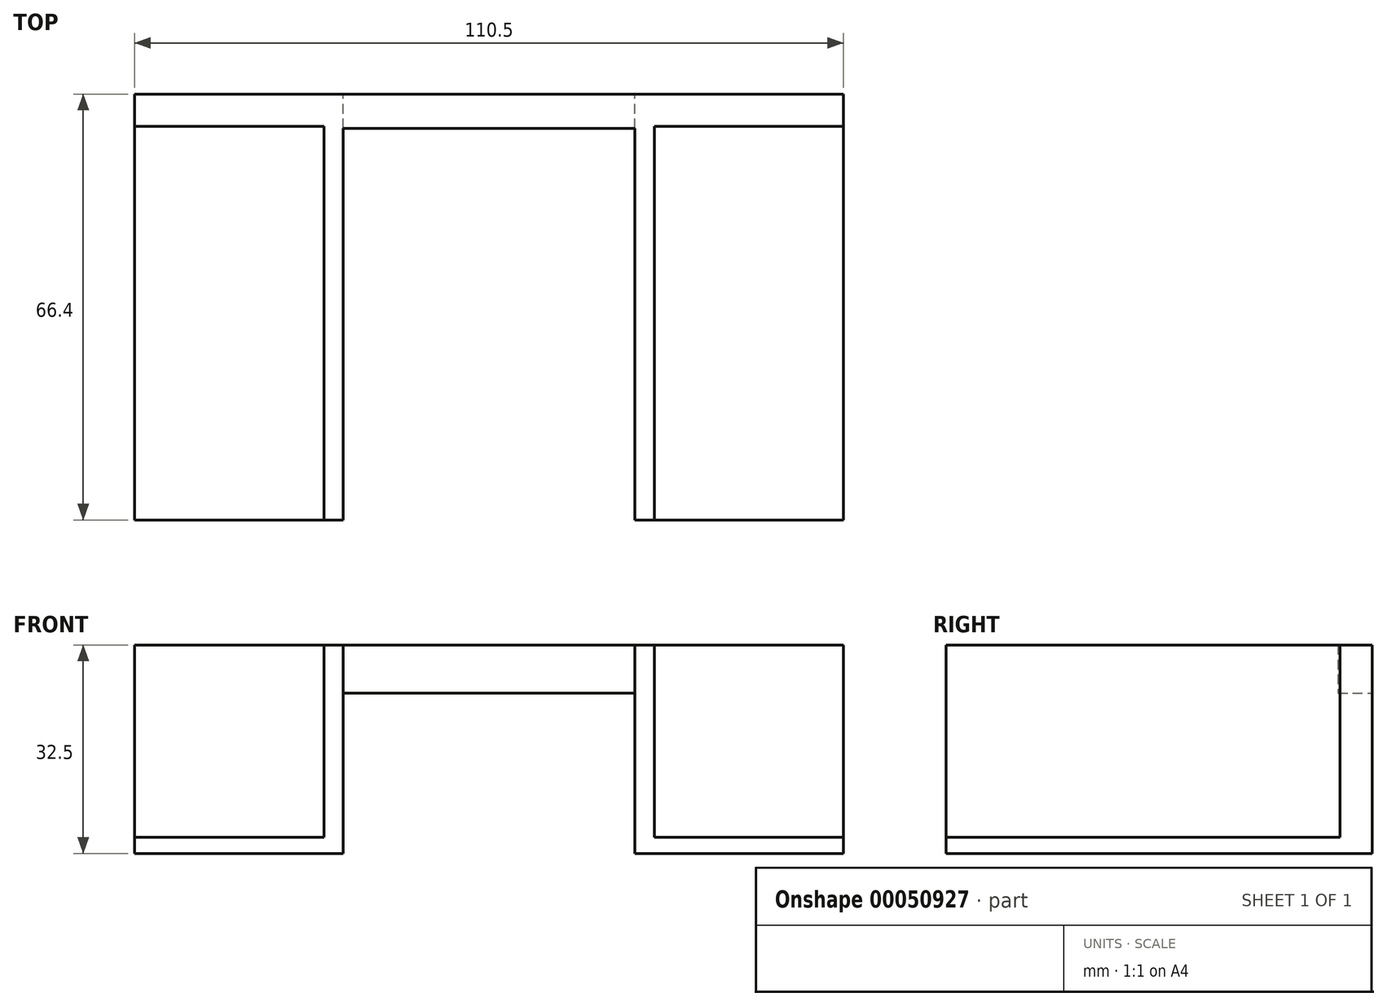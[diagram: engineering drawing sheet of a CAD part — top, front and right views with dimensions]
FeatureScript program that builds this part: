
annotation { "Feature Type Name" : "Feature", "Feature Type Description" : "" }
export const myFeature = defineFeature(function(context is Context, id is Id, definition is map)
    precondition{}
    {
        {
            var Q0;
            Q0=qCreatedBy(makeId("Top.planeOp"),FACE);
            var sketch = newSketch(context, id + "F0", { "sketchPlane" : qUnion([Q0])});
            skLineSegment(sketch, "E0", {"start": v(-58.03, 30.15) * mm, "end": v(-58.03, 30.15) * mm});
            skLineSegment(sketch, "E1", {"start": v(-58.03, 30.15) * mm, "end": v(-58.03, 36.65) * mm});
            skLineSegment(sketch, "E2", {"start": v(-58.03, 36.65) * mm, "end": v(-51.53, 36.65) * mm});
            skLineSegment(sketch, "E3", {"start": v(-51.53, 36.65) * mm, "end": v(-51.53, 30.15) * mm});
            skLineSegment(sketch, "E4", {"start": v(-51.53, 30.15) * mm, "end": v(-45.03, 30.15) * mm});
            skLineSegment(sketch, "E5", {"start": v(-45.03, 30.15) * mm, "end": v(-45.03, 36.65) * mm});
            skLineSegment(sketch, "E6", {"start": v(-45.03, 36.65) * mm, "end": v(-38.53, 36.65) * mm});
            skLineSegment(sketch, "E7", {"start": v(-38.53, 36.65) * mm, "end": v(-38.53, 30.15) * mm});
            skLineSegment(sketch, "E8", {"start": v(-38.53, 30.15) * mm, "end": v(-32.03, 30.15) * mm});
            skLineSegment(sketch, "E9", {"start": v(-32.03, 30.15) * mm, "end": v(-32.03, 36.65) * mm});
            skLineSegment(sketch, "E10", {"start": v(-32.03, 36.65) * mm, "end": v(-25.53, 36.65) * mm});
            skLineSegment(sketch, "E11", {"start": v(-25.53, 36.65) * mm, "end": v(-25.53, 30.15) * mm});
            skLineSegment(sketch, "E12", {"start": v(-25.53, 30.15) * mm, "end": v(-19.03, 30.15) * mm});
            skLineSegment(sketch, "E13", {"start": v(-19.03, 30.15) * mm, "end": v(-19.03, 36.65) * mm});
            skLineSegment(sketch, "E14", {"start": v(-19.03, 36.65) * mm, "end": v(-12.53, 36.65) * mm});
            skLineSegment(sketch, "E15", {"start": v(-12.53, 36.65) * mm, "end": v(-12.53, 30.15) * mm});
            skLineSegment(sketch, "E16", {"start": v(-12.53, 30.15) * mm, "end": v(-6.03, 30.15) * mm});
            skLineSegment(sketch, "E17", {"start": v(-6.03, 30.15) * mm, "end": v(-6.03, 36.65) * mm});
            skLineSegment(sketch, "E18", {"start": v(0.47, 36.65) * mm, "end": v(0.47, 30.15) * mm});
            skLineSegment(sketch, "E19", {"start": v(0.47, 30.15) * mm, "end": v(6.97, 30.15) * mm});
            skLineSegment(sketch, "E20", {"start": v(6.97, 30.15) * mm, "end": v(6.97, 36.65) * mm});
            skLineSegment(sketch, "E21", {"start": v(6.97, 36.65) * mm, "end": v(13.47, 36.65) * mm});
            skLineSegment(sketch, "E22", {"start": v(13.47, 36.65) * mm, "end": v(13.47, 30.15) * mm});
            skLineSegment(sketch, "E23", {"start": v(13.47, 30.15) * mm, "end": v(19.97, 30.15) * mm});
            skLineSegment(sketch, "E24", {"start": v(19.97, 30.15) * mm, "end": v(19.97, 36.65) * mm});
            skLineSegment(sketch, "E25", {"start": v(19.97, 36.65) * mm, "end": v(26.47, 36.65) * mm});
            skLineSegment(sketch, "E26", {"start": v(26.47, 36.65) * mm, "end": v(26.47, 30.15) * mm});
            skLineSegment(sketch, "E27", {"start": v(26.47, 30.15) * mm, "end": v(32.97, 30.15) * mm});
            skLineSegment(sketch, "E28", {"start": v(32.97, 30.15) * mm, "end": v(32.97, 36.65) * mm});
            skLineSegment(sketch, "E29", {"start": v(32.97, 36.65) * mm, "end": v(39.47, 36.65) * mm});
            skLineSegment(sketch, "E30", {"start": v(39.47, 36.65) * mm, "end": v(39.47, 30.15) * mm});
            skLineSegment(sketch, "E31", {"start": v(39.47, 30.15) * mm, "end": v(45.97, 30.15) * mm});
            skLineSegment(sketch, "E32", {"start": v(45.97, 30.15) * mm, "end": v(45.97, 36.65) * mm});
            skLineSegment(sketch, "E33", {"start": v(45.97, 36.65) * mm, "end": v(52.47, 36.65) * mm});
            skLineSegment(sketch, "E34", {"start": v(52.47, 36.65) * mm, "end": v(52.47, 30.15) * mm});
            skLineSegment(sketch, "E35", {"start": v(52.47, 30.15) * mm, "end": v(58.97, 30.15) * mm});
            skLineSegment(sketch, "E36", {"start": v(-6.03, 36.65) * mm, "end": v(0.47, 36.65) * mm});
            skLineSegment(sketch, "E37", {"start": v(-64.53, 30.15) * mm, "end": v(-58.03, 30.15) * mm});
            skLineSegment(sketch, "E38", {"start": v(58.97, 30.15) * mm, "end": v(58.97, 23.65) * mm});
            skLineSegment(sketch, "E39", {"start": v(58.97, 23.65) * mm, "end": v(58.97, 17.15) * mm});
            skLineSegment(sketch, "E40", {"start": v(58.97, 17.15) * mm, "end": v(65.47, 17.15) * mm});
            skLineSegment(sketch, "E41", {"start": v(65.47, 17.15) * mm, "end": v(65.47, 10.65) * mm});
            skLineSegment(sketch, "E42", {"start": v(65.47, 10.65) * mm, "end": v(58.97, 10.65) * mm});
            skLineSegment(sketch, "E43", {"start": v(58.97, 10.65) * mm, "end": v(58.97, 4.15) * mm});
            skLineSegment(sketch, "E44", {"start": v(58.97, 4.15) * mm, "end": v(65.47, 4.15) * mm});
            skLineSegment(sketch, "E45", {"start": v(65.47, 4.15) * mm, "end": v(65.47, -2.35) * mm});
            skLineSegment(sketch, "E46", {"start": v(65.47, -2.35) * mm, "end": v(58.97, -2.35) * mm});
            skLineSegment(sketch, "E47", {"start": v(58.97, -2.35) * mm, "end": v(58.97, -8.85) * mm});
            skLineSegment(sketch, "E48", {"start": v(58.97, -8.85) * mm, "end": v(65.47, -8.85) * mm});
            skLineSegment(sketch, "E49", {"start": v(65.47, -8.85) * mm, "end": v(65.47, -15.35) * mm});
            skLineSegment(sketch, "E50", {"start": v(65.47, -15.35) * mm, "end": v(58.97, -15.35) * mm});
            skLineSegment(sketch, "E51", {"start": v(58.97, -15.35) * mm, "end": v(58.97, -21.85) * mm});
            skLineSegment(sketch, "E52", {"start": v(58.97, -21.85) * mm, "end": v(65.47, -21.85) * mm});
            skLineSegment(sketch, "E53", {"start": v(65.47, -21.85) * mm, "end": v(65.47, -28.35) * mm});
            skLineSegment(sketch, "E54", {"start": v(65.47, -28.35) * mm, "end": v(58.97, -28.35) * mm});
            skLineSegment(sketch, "E55", {"start": v(58.97, -28.35) * mm, "end": v(58.97, -34.85) * mm});
            skLineSegment(sketch, "E56", {"start": v(58.97, -34.85) * mm, "end": v(65.47, -34.85) * mm});
            skLineSegment(sketch, "E57", {"start": v(65.47, -34.85) * mm, "end": v(65.47, -41.35) * mm});
            skLineSegment(sketch, "E58", {"start": v(65.47, -41.35) * mm, "end": v(58.97, -41.35) * mm});
            skLineSegment(sketch, "E59.MirrorCS", {"start": v(-64.53, -34.85) * mm, "end": v(-64.53, -41.35) * mm});
            skLineSegment(sketch, "E60.MirrorCS", {"start": v(-64.53, -21.85) * mm, "end": v(-64.53, -28.35) * mm});
            skLineSegment(sketch, "E61.MirrorCS", {"start": v(-58.03, -34.85) * mm, "end": v(-64.53, -34.85) * mm});
            skLineSegment(sketch, "E62.MirrorCS", {"start": v(-58.03, -2.35) * mm, "end": v(-58.03, -8.85) * mm});
            skLineSegment(sketch, "E63.MirrorCS", {"start": v(-64.53, -2.35) * mm, "end": v(-58.03, -2.35) * mm});
            skLineSegment(sketch, "E64.MirrorCS", {"start": v(-58.03, -28.35) * mm, "end": v(-58.03, -34.85) * mm});
            skLineSegment(sketch, "E65.MirrorCS", {"start": v(-58.03, 4.15) * mm, "end": v(-64.53, 4.15) * mm});
            skLineSegment(sketch, "E66.MirrorCS", {"start": v(-64.53, -41.35) * mm, "end": v(-58.03, -41.35) * mm});
            skLineSegment(sketch, "E67.MirrorCS", {"start": v(-64.53, 4.15) * mm, "end": v(-64.53, -2.35) * mm});
            skLineSegment(sketch, "E68.MirrorCS", {"start": v(-64.53, -8.85) * mm, "end": v(-64.53, -15.35) * mm});
            skLineSegment(sketch, "E69.MirrorCS", {"start": v(-58.03, 10.65) * mm, "end": v(-58.03, 4.15) * mm});
            skLineSegment(sketch, "E70.MirrorCS", {"start": v(-58.03, -15.35) * mm, "end": v(-58.03, -21.85) * mm});
            skLineSegment(sketch, "E71.MirrorCS", {"start": v(-64.53, -15.35) * mm, "end": v(-58.03, -15.35) * mm});
            skLineSegment(sketch, "E72.MirrorCS", {"start": v(-58.03, -8.85) * mm, "end": v(-64.53, -8.85) * mm});
            skLineSegment(sketch, "E73.MirrorCS", {"start": v(-64.53, -28.35) * mm, "end": v(-58.03, -28.35) * mm});
            skLineSegment(sketch, "E74.MirrorCS", {"start": v(-58.03, -21.85) * mm, "end": v(-64.53, -21.85) * mm});
            skLineSegment(sketch, "E75.MirrorCS", {"start": v(-64.53, 10.65) * mm, "end": v(-58.03, 10.65) * mm});
            skLineSegment(sketch, "E76.MirrorCS", {"start": v(-58.03, 17.15) * mm, "end": v(-64.53, 17.15) * mm});
            skLineSegment(sketch, "E77.MirrorCS", {"start": v(-64.53, 17.15) * mm, "end": v(-64.53, 10.65) * mm});
            skLineSegment(sketch, "E78", {"start": v(-58.03, 17.15) * mm, "end": v(-58.03, 23.65) * mm});
            skLineSegment(sketch, "E79", {"start": v(-58.03, 23.65) * mm, "end": v(-64.53, 23.65) * mm});
            skLineSegment(sketch, "E80", {"start": v(-64.53, 23.65) * mm, "end": v(-64.53, 30.15) * mm});
            skLineSegment(sketch, "E81", {"start": v(-58.03, -41.35) * mm, "end": v(-58.03, -53.45) * mm});
            skLineSegment(sketch, "E82", {"start": v(58.97, -41.35) * mm, "end": v(58.97, -53.45) * mm});
            skLineSegment(sketch, "E83", {"start": v(-58.03, -53.45) * mm, "end": v(58.97, -53.45) * mm});
            skLineSegment(sketch, "E84.bottom", {"start": v(114.02, 15.34) * mm, "end": v(224.52, 15.34) * mm});
            skLineSegment(sketch, "E84.top", {"start": v(114.02, -51.06) * mm, "end": v(224.52, -51.06) * mm});
            skLineSegment(sketch, "E84.left", {"start": v(114.02, 15.34) * mm, "end": v(114.02, -51.06) * mm});
            skLineSegment(sketch, "E84.right", {"start": v(224.52, 15.34) * mm, "end": v(224.52, -51.06) * mm});
            skLineSegment(sketch, "E85", {"start": v(114.02, 10.34) * mm, "end": v(143.52, 10.34) * mm});
            skLineSegment(sketch, "E86", {"start": v(143.52, 10.34) * mm, "end": v(143.52, -51.06) * mm});
            skLineSegment(sketch, "E87", {"start": v(224.52, 10.34) * mm, "end": v(195.02, 10.34) * mm});
            skLineSegment(sketch, "E88", {"start": v(195.02, 10.34) * mm, "end": v(195.02, -51.06) * mm});
            skLineSegment(sketch, "E89", {"start": v(146.52, -51.06) * mm, "end": v(146.52, 10.02) * mm});
            skLineSegment(sketch, "E90", {"start": v(146.52, 10.02) * mm, "end": v(192.02, 10.02) * mm});
            skLineSegment(sketch, "E91", {"start": v(192.02, 10.02) * mm, "end": v(192.02, -51.06) * mm});
            skSolve(sketch);
        }
        {
            var Q0;
            Q0=makeQuery(id+"F0.imprint","IMPRINT",FACE,{"disambiguationData":[TD([[makeQuery(id+"F0.imprint","IMPRINT",EDGE,{"derivedFrom":sQuery(id+"F0.wireOp",EDGE,"E1")}),-1.0]])]});
            extrude(context, id + "F1", {"entities" : qUnion([Q0]), "depth" : 6.5 * mm});
        }
        {
            var Q0;
            {var subQ1=sQuery(id+"F0.wireOp",EDGE,"E84.bottom");Q0=makeQuery(id+"F0.imprint","IMPRINT",FACE,{"disambiguationData":[TD([[makeQuery(id+"F0.imprint","IMPRINT",EDGE,{"derivedFrom":subQ1}),-1.0]])]});}
            extrude(context, id + "F2", {"entities" : qUnion([Q0]), "depth" : 30 * mm});
        }
        {
            var Q0;
            Q0=makeQuery(id+"F2.opExtrude","CAP_FACE",FACE,{"disambiguationData":[OSD([sQuery(id+"F0.wireOp",EDGE,"E84.bottom"),sQuery(id+"F0.wireOp",EDGE,"E84.top"),sQuery(id+"F0.wireOp",EDGE,"E84.left"),sQuery(id+"F0.wireOp",EDGE,"E84.right"),sQuery(id+"F0.wireOp",EDGE,"E85"),sQuery(id+"F0.wireOp",EDGE,"E86"),sQuery(id+"F0.wireOp",EDGE,"E87"),sQuery(id+"F0.wireOp",EDGE,"E88")])],"isStart":true});
            extrude(context, id + "F3", {"entities" : qUnion([Q0]), "operationType" : NewBodyOperationType.ADD, "depth" : 2.5 * mm});
        }
        {
            var Q0;
            {var subQ4=sQuery(id+"F0.wireOp",EDGE,"E87");Q0=makeQuery(id+"F0.imprint","IMPRINT",FACE,{"disambiguationData":[TD([[makeQuery(id+"F0.imprint","IMPRINT",EDGE,{"derivedFrom":subQ4}),1.0]])]});}
            var Q1;
            {var subQ4=sQuery(id+"F0.wireOp",EDGE,"E85");Q1=makeQuery(id+"F0.imprint","IMPRINT",FACE,{"disambiguationData":[TD([[makeQuery(id+"F0.imprint","IMPRINT",EDGE,{"derivedFrom":subQ4}),-1.0]])]});}
            extrude(context, id + "F4", {"entities" : qUnion([Q0, Q1]), "operationType" : NewBodyOperationType.ADD, "oppositeDirection" : true, "depth" : 2.5 * mm});
        }
        {
            var Q0;
            {var subQ0=sQuery(id+"F0.wireOp",EDGE,"E88");var subQ1=sQuery(id+"F0.wireOp",EDGE,"E87");var subQ2=sQuery(id+"F0.wireOp",EDGE,"E84.right");var subQ3=sQuery(id+"F0.wireOp",EDGE,"E84.top");var subQ4=sQuery(id+"F0.wireOp",EDGE,"E86");var subQ5=sQuery(id+"F0.wireOp",EDGE,"E85");var subQ6=sQuery(id+"F0.wireOp",EDGE,"E84.left");Q0=makeQuery(id+"F4.boolean.opBoolean","MERGE",FACE,{"derivedFrom":[makeQuery(id+"F3.opExtrude","CAP_FACE",FACE,{"disambiguationData":[OSD([sQuery(id+"F0.wireOp",EDGE,"E84.bottom"),subQ3,subQ6,subQ2,subQ5,subQ4,subQ1,subQ0,sQuery(id+"F0.wireOp",EDGE,"E89"),sQuery(id+"F0.wireOp",EDGE,"E90"),sQuery(id+"F0.wireOp",EDGE,"E91")])],"isStart":false}),makeQuery(id+"F4.opExtrude","CAP_FACE",FACE,{"disambiguationData":[OSD([subQ3,subQ6,subQ5,subQ4])],"isStart":false}),makeQuery(id+"F4.opExtrude","CAP_FACE",FACE,{"disambiguationData":[OSD([subQ3,subQ2,subQ1,subQ0])],"isStart":false})]});}
            var sketch = newSketch(context, id + "F5", { "sketchPlane" : qUnion([Q0])});
            skLineSegment(sketch, "E92", {"start": v(146.52, -10.02) * mm, "end": v(146.52, -15.34) * mm});
            skLineSegment(sketch, "E93", {"start": v(192.02, -10.02) * mm, "end": v(192.02, -15.34) * mm});
            skSolve(sketch);
        }
        {
            var Q0;
            {var subQ0=sQuery(id+"F5.wireOp",EDGE,"E92");Q0=makeQuery(id+"F5.imprint","IMPRINT",FACE,{"disambiguationData":[TD([[makeQuery(id+"F5.imprint","IMPRINT",EDGE,{"derivedFrom":subQ0}),1.0]])]});}
            extrude(context, id + "F6", {"entities" : qUnion([Q0]), "operationType" : NewBodyOperationType.REMOVE, "oppositeDirection" : true, "depth" : 25 * mm});
        }
        {
            var Q0;
            Q0=makeQuery(id+"F2.opExtrude","SWEPT_BODY",BODY,{"disambiguationData":[OSD([sQuery(id+"F0.wireOp",EDGE,"E84.bottom"),sQuery(id+"F0.wireOp",EDGE,"E84.top"),sQuery(id+"F0.wireOp",EDGE,"E84.left"),sQuery(id+"F0.wireOp",EDGE,"E84.right"),sQuery(id+"F0.wireOp",EDGE,"E85"),sQuery(id+"F0.wireOp",EDGE,"E86"),sQuery(id+"F0.wireOp",EDGE,"E87"),sQuery(id+"F0.wireOp",EDGE,"E88"),sQuery(id+"F0.wireOp",EDGE,"E89"),sQuery(id+"F0.wireOp",EDGE,"E90"),sQuery(id+"F0.wireOp",EDGE,"E91")])]});
            transform(context, id + "F7", {"entities" : qUnion([Q0]), "transformType" : TransformType.TRANSLATION_3D, "dx" : 0 * mm, "dy" : 0 * mm, "dz" : 0 * mm, "makeCopy" : true});
        }
        {
            var Q0;
            Q0=makeQuery(id+"F2.opExtrude","SWEPT_BODY",BODY,{"disambiguationData":[OSD([sQuery(id+"F0.wireOp",EDGE,"E84.bottom"),sQuery(id+"F0.wireOp",EDGE,"E84.top"),sQuery(id+"F0.wireOp",EDGE,"E84.left"),sQuery(id+"F0.wireOp",EDGE,"E84.right"),sQuery(id+"F0.wireOp",EDGE,"E85"),sQuery(id+"F0.wireOp",EDGE,"E86"),sQuery(id+"F0.wireOp",EDGE,"E87"),sQuery(id+"F0.wireOp",EDGE,"E88"),sQuery(id+"F0.wireOp",EDGE,"E89"),sQuery(id+"F0.wireOp",EDGE,"E90"),sQuery(id+"F0.wireOp",EDGE,"E91")])]});
            var Q1;
            Q1=makeQuery(id+"F1.opExtrude","SWEPT_BODY",BODY,{"disambiguationData":[OSD([sQuery(id+"F0.wireOp",EDGE,"E1"),sQuery(id+"F0.wireOp",EDGE,"E2"),sQuery(id+"F0.wireOp",EDGE,"E3"),sQuery(id+"F0.wireOp",EDGE,"E4"),sQuery(id+"F0.wireOp",EDGE,"E5"),sQuery(id+"F0.wireOp",EDGE,"E6"),sQuery(id+"F0.wireOp",EDGE,"E7"),sQuery(id+"F0.wireOp",EDGE,"E8"),sQuery(id+"F0.wireOp",EDGE,"E9"),sQuery(id+"F0.wireOp",EDGE,"E10"),sQuery(id+"F0.wireOp",EDGE,"E11"),sQuery(id+"F0.wireOp",EDGE,"E12"),sQuery(id+"F0.wireOp",EDGE,"E13"),sQuery(id+"F0.wireOp",EDGE,"E14"),sQuery(id+"F0.wireOp",EDGE,"E15"),sQuery(id+"F0.wireOp",EDGE,"E16"),sQuery(id+"F0.wireOp",EDGE,"E17"),sQuery(id+"F0.wireOp",EDGE,"E18"),sQuery(id+"F0.wireOp",EDGE,"E19"),sQuery(id+"F0.wireOp",EDGE,"E20"),sQuery(id+"F0.wireOp",EDGE,"E21"),sQuery(id+"F0.wireOp",EDGE,"E22"),sQuery(id+"F0.wireOp",EDGE,"E23"),sQuery(id+"F0.wireOp",EDGE,"E24"),sQuery(id+"F0.wireOp",EDGE,"E25"),sQuery(id+"F0.wireOp",EDGE,"E26"),sQuery(id+"F0.wireOp",EDGE,"E27"),sQuery(id+"F0.wireOp",EDGE,"E28"),sQuery(id+"F0.wireOp",EDGE,"E29"),sQuery(id+"F0.wireOp",EDGE,"E30"),sQuery(id+"F0.wireOp",EDGE,"E31"),sQuery(id+"F0.wireOp",EDGE,"E32"),sQuery(id+"F0.wireOp",EDGE,"E33"),sQuery(id+"F0.wireOp",EDGE,"E34"),sQuery(id+"F0.wireOp",EDGE,"E35"),sQuery(id+"F0.wireOp",EDGE,"E36"),sQuery(id+"F0.wireOp",EDGE,"E37"),sQuery(id+"F0.wireOp",EDGE,"E38"),sQuery(id+"F0.wireOp",EDGE,"E39"),sQuery(id+"F0.wireOp",EDGE,"E40"),sQuery(id+"F0.wireOp",EDGE,"E41"),sQuery(id+"F0.wireOp",EDGE,"E42"),sQuery(id+"F0.wireOp",EDGE,"E43"),sQuery(id+"F0.wireOp",EDGE,"E44"),sQuery(id+"F0.wireOp",EDGE,"E45"),sQuery(id+"F0.wireOp",EDGE,"E46"),sQuery(id+"F0.wireOp",EDGE,"E47"),sQuery(id+"F0.wireOp",EDGE,"E48"),sQuery(id+"F0.wireOp",EDGE,"E49"),sQuery(id+"F0.wireOp",EDGE,"E50"),sQuery(id+"F0.wireOp",EDGE,"E51"),sQuery(id+"F0.wireOp",EDGE,"E52"),sQuery(id+"F0.wireOp",EDGE,"E53"),sQuery(id+"F0.wireOp",EDGE,"E54"),sQuery(id+"F0.wireOp",EDGE,"E55"),sQuery(id+"F0.wireOp",EDGE,"E56"),sQuery(id+"F0.wireOp",EDGE,"E57"),sQuery(id+"F0.wireOp",EDGE,"E58"),sQuery(id+"F0.wireOp",EDGE,"E59.MirrorCS"),sQuery(id+"F0.wireOp",EDGE,"E60.MirrorCS"),sQuery(id+"F0.wireOp",EDGE,"E61.MirrorCS"),sQuery(id+"F0.wireOp",EDGE,"E62.MirrorCS"),sQuery(id+"F0.wireOp",EDGE,"E63.MirrorCS"),sQuery(id+"F0.wireOp",EDGE,"E64.MirrorCS"),sQuery(id+"F0.wireOp",EDGE,"E65.MirrorCS"),sQuery(id+"F0.wireOp",EDGE,"E66.MirrorCS"),sQuery(id+"F0.wireOp",EDGE,"E67.MirrorCS"),sQuery(id+"F0.wireOp",EDGE,"E68.MirrorCS"),sQuery(id+"F0.wireOp",EDGE,"E69.MirrorCS"),sQuery(id+"F0.wireOp",EDGE,"E70.MirrorCS"),sQuery(id+"F0.wireOp",EDGE,"E71.MirrorCS"),sQuery(id+"F0.wireOp",EDGE,"E72.MirrorCS"),sQuery(id+"F0.wireOp",EDGE,"E73.MirrorCS"),sQuery(id+"F0.wireOp",EDGE,"E74.MirrorCS"),sQuery(id+"F0.wireOp",EDGE,"E75.MirrorCS"),sQuery(id+"F0.wireOp",EDGE,"E76.MirrorCS"),sQuery(id+"F0.wireOp",EDGE,"E77.MirrorCS"),sQuery(id+"F0.wireOp",EDGE,"E78"),sQuery(id+"F0.wireOp",EDGE,"E79"),sQuery(id+"F0.wireOp",EDGE,"E80"),sQuery(id+"F0.wireOp",EDGE,"E81"),sQuery(id+"F0.wireOp",EDGE,"E82"),sQuery(id+"F0.wireOp",EDGE,"E83")])]});
            deleteBodies(context, id + "F8", {"entities" : qUnion([Q0, Q1])});
        }
    });
